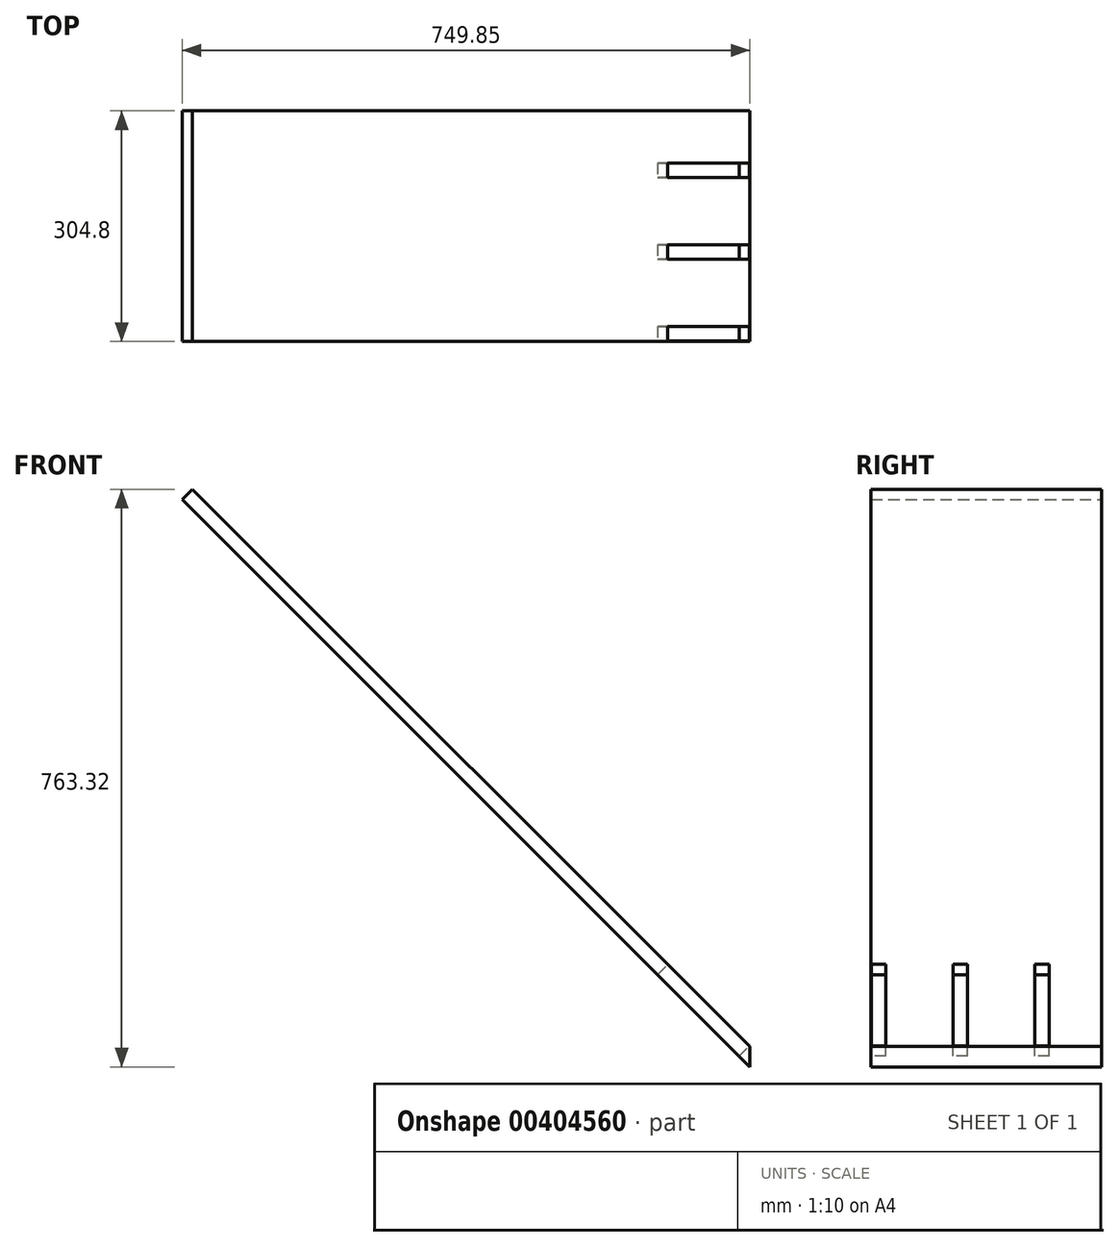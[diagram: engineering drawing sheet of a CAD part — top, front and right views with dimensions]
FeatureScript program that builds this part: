
annotation { "Feature Type Name" : "Feature", "Feature Type Description" : "" }
export const myFeature = defineFeature(function(context is Context, id is Id, definition is map)
    precondition{}
    {
        {
            var Q0;
            Q0=qCreatedBy(makeId("Front.planeOp"),FACE);
            var sketch = newSketch(context, id + "F0", { "sketchPlane" : qUnion([Q0])});
            skLineSegment(sketch, "E0.MirrorCS", {"start": v(378.53, 134.65) * mm, "end": v(-371.32, 884.5) * mm});
            skLineSegment(sketch, "E1.MirrorCS", {"start": v(378.53, 161.6) * mm, "end": v(-357.85, 897.97) * mm});
            skLineSegment(sketch, "E2.MirrorCS", {"start": v(378.53, 134.65) * mm, "end": v(378.53, 161.6) * mm});
            skLineSegment(sketch, "E3", {"start": v(-357.85, 897.97) * mm, "end": v(-371.32, 884.5) * mm});
            skSolve(sketch);
        }
        {
            var Q0;
            Q0=qSketchRegion(id+"F0",true);
            extrude(context, id + "F1", {"entities" : qUnion([Q0]), "endBound" : BoundingType.SYMMETRIC, "depth" : 304.8 * mm});
        }
        {
            var Q0;
            Q0=makeQuery(id+"F1.opExtrude","SWEPT_FACE",FACE,{"disambiguationData":[OSD([sQuery(id+"F0.wireOp",EDGE,"E1.MirrorCS")])]});
            var sketch = newSketch(context, id + "F2", { "sketchPlane" : qUnion([Q0])});
            skLineSegment(sketch, "E4.bottom", {"start": v(83.55, -152.4) * mm, "end": v(64.5, -152.4) * mm});
            skLineSegment(sketch, "E4.top", {"start": v(83.55, 0) * mm, "end": v(64.5, 0) * mm});
            skLineSegment(sketch, "E4.left", {"start": v(83.55, -152.4) * mm, "end": v(83.55, 0) * mm});
            skLineSegment(sketch, "E4.right", {"start": v(64.5, -152.4) * mm, "end": v(64.5, 0) * mm});
            skLineSegment(sketch, "E5.bottom", {"start": v(-24.4, -152.4) * mm, "end": v(-43.45, -152.4) * mm});
            skLineSegment(sketch, "E5.top", {"start": v(-24.4, 0) * mm, "end": v(-43.45, 0) * mm});
            skLineSegment(sketch, "E5.left", {"start": v(-24.4, -152.4) * mm, "end": v(-24.4, 0) * mm});
            skLineSegment(sketch, "E5.right", {"start": v(-43.45, -152.4) * mm, "end": v(-43.45, 0) * mm});
            skLineSegment(sketch, "E6.bottom", {"start": v(-132.35, -152.4) * mm, "end": v(-151.4, -152.4) * mm});
            skLineSegment(sketch, "E6.top", {"start": v(-132.35, 0) * mm, "end": v(-151.4, 0) * mm});
            skLineSegment(sketch, "E6.left", {"start": v(-132.35, -152.4) * mm, "end": v(-132.35, 0) * mm});
            skLineSegment(sketch, "E6.right", {"start": v(-151.4, -152.4) * mm, "end": v(-151.4, 0) * mm});
            skLineSegment(sketch, "E7.bottom", {"start": v(-240.3, -152.4) * mm, "end": v(-259.35, -152.4) * mm});
            skLineSegment(sketch, "E7.top", {"start": v(-240.3, 0) * mm, "end": v(-259.35, 0) * mm});
            skLineSegment(sketch, "E7.left", {"start": v(-240.3, -152.4) * mm, "end": v(-240.3, 0) * mm});
            skLineSegment(sketch, "E7.right", {"start": v(-259.35, -152.4) * mm, "end": v(-259.35, 0) * mm});
            skLineSegment(sketch, "E8.bottom", {"start": v(-348.25, -152.4) * mm, "end": v(-367.3, -152.4) * mm});
            skLineSegment(sketch, "E8.top", {"start": v(-348.25, 0) * mm, "end": v(-367.3, 0) * mm});
            skLineSegment(sketch, "E8.left", {"start": v(-348.25, -152.4) * mm, "end": v(-348.25, 0) * mm});
            skLineSegment(sketch, "E8.right", {"start": v(-367.3, -152.4) * mm, "end": v(-367.3, 0) * mm});
            skLineSegment(sketch, "E9.bottom", {"start": v(-456.2, -152.4) * mm, "end": v(-475.25, -152.4) * mm});
            skLineSegment(sketch, "E9.top", {"start": v(-456.2, 0) * mm, "end": v(-475.25, 0) * mm});
            skLineSegment(sketch, "E9.left", {"start": v(-456.2, -152.4) * mm, "end": v(-456.2, 0) * mm});
            skLineSegment(sketch, "E9.right", {"start": v(-475.25, -152.4) * mm, "end": v(-475.25, 0) * mm});
            skLineSegment(sketch, "E10.bottom", {"start": v(-564.15, -152.4) * mm, "end": v(-583.2, -152.4) * mm});
            skLineSegment(sketch, "E10.top", {"start": v(-564.15, 0) * mm, "end": v(-583.2, 0) * mm});
            skLineSegment(sketch, "E10.left", {"start": v(-564.15, -152.4) * mm, "end": v(-564.15, 0) * mm});
            skLineSegment(sketch, "E10.right", {"start": v(-583.2, -152.4) * mm, "end": v(-583.2, 0) * mm});
            skLineSegment(sketch, "E11.bottom", {"start": v(-672.1, -152.4) * mm, "end": v(-691.15, -152.4) * mm});
            skLineSegment(sketch, "E11.top", {"start": v(-672.1, 0) * mm, "end": v(-691.15, 0) * mm});
            skLineSegment(sketch, "E11.left", {"start": v(-672.1, -152.4) * mm, "end": v(-672.1, 0) * mm});
            skLineSegment(sketch, "E11.right", {"start": v(-691.15, -152.4) * mm, "end": v(-691.15, 0) * mm});
            skLineSegment(sketch, "E12.bottom", {"start": v(-780.05, -152.4) * mm, "end": v(-799.1, -152.4) * mm});
            skLineSegment(sketch, "E12.top", {"start": v(-780.05, 0) * mm, "end": v(-799.1, 0) * mm});
            skLineSegment(sketch, "E12.left", {"start": v(-780.05, -152.4) * mm, "end": v(-780.05, 0) * mm});
            skLineSegment(sketch, "E12.right", {"start": v(-799.1, -152.4) * mm, "end": v(-799.1, 0) * mm});
            skSolve(sketch);
        }
        {
            var Q0;
            Q0 = qSketchRegion(id + "F2", true);
            extrude(context, id + "F3", {"entities" : qUnion([Q0]), "operationType" : NewBodyOperationType.REMOVE, "oppositeDirection" : true, "depth" : 19.05 * mm});
        }
    });
